# Revit family: 280 NonAutomatic Series
name_source: partatom
category: Mechanical Equipment
revit_build: Autodesk Revit 2013 (Build: 20120221_2030(x64)
units: mm (PartAtom-declared; Revit-internal decimal feet)

## types (13) — shared parameters
Assembly Code = D2010900
Cooling = Oil Filled
Cord Length = 180"
Cord Type = UL listed, 3-wire neoprene cord and plug (1 Ph) or 4-wire cord with no plug (3 Ph)
Default Elevation = 0"
Description = Single Seal Non-Automatic Submersible Sewage or Dewatering Pumps
Discharge Diameter = 2" or 3" NPT Female, Flanged Vertical
Discharge Height = 6 1/4"
Discharge Radius = 1"
Height = 19 9/16"
Hertz = 60
Impeller = Cast Iron
Impeller Type = Non-clogging vortex
Installation Type = Floor Mounted
Insulation = Class B
Lead Wires Insulation = Class B
Length = 13 9/16"
Manufacturer = Zoeller
Masterformat Number = 33 36 16
Masterformat Title = Utility Septic Tank Effluent Pumps
Material = Cast Iron-Zoeller-Powder Coated Epoxy
Max. Operating Temp. = 130.00 °F
Mechanical Seals = Carbon and Ceramic
Minimum Head = 60"
Motor Thermal Shutoff (Single Phase Only) = Thermal Overload Sensors With Automatic Reset.
Motor Type = Submersible
Omniclass Table 23 Code = 23.60.30.21
Omniclass Table 23 Title = Pumps
Operation = Non-Automatic
Price = Prices may vary. Please consult Manufacturer Representative for most up-to-date price list.
Product Page URL = http://www.zoellerpumps.com
RPM = 1725
Shipping Weight = 80 lbs
Solid Handling = 2" Spherical Solids
Square Ring & Gasket = Neoprene
Type Comments = Available in single or double seal designs.
URL = http://www.zoellerpumps.com
Warranty Information = 36 Months (Limited)
Waste Connection = Yes
Width = 10"

## per-type parameters (varying)
| type | Amps | Apparent Load | Flow @ 5' | Maximum Head | Model | Motor | Phase | Type | Voltage |
| 282-115V 1Ph | 10 A | 1185 VA | 127 GPM | 312" | 282 | 1/2 HP | 1 | Permanent Split Capacitor | 115 V |
| 282-230V 1Ph | 5 A | 1150 VA | 127 GPM | 312" | 282 | 1/2 HP | 1 | Permanent Split Capacitor | 230 V |
| 282-200V 1Ph | 6 A | 1220 VA | 127 GPM | 312" | 282 | 1/2 HP | 1 | Permanent Split Capacitor | 200 V |
| 282-200V 3Ph | 4 A | 720 VA | 127 GPM | 312" | 282 | 1/2 HP | 3 Ph | 3 Phase | 200 V |
| 282-230V 3Ph | 3 A | 690 VA | 127 GPM | 312" | 282 | 1/2 HP | 3 Ph | 3 Phase | 230 V |
| 282-460V 3Ph | 2 A | 782 VA | 127 GPM | 312" | 282 | 1/2 HP | 3 Ph | 3 Phase | 460 V |
| 282-575V 3Ph | 1 A | 805 VA | 127 GPM | 312" | 282 | 1/2 HP | 3 Ph | 3 Phase | 575 V |
| 284-230V 1Ph | 9 A | 2047 VA | 179 GPM | 420" | 284 | 1 HP | 1 | Permanent Split Capacitor | 230 V |
| 284-200V 1Ph | 9 A | 1860 VA | 179 GPM | 420" | 284 | 1 HP | 1 | Permanent Split Capacitor | 200 V |
| 284-200V 3Ph | 6 A | 1100 VA | 179 GPM | 420" | 284 | 1 HP | 3 Ph | 3 Phase | 200 V |
| 284-230V 3Ph | 5 A | 1150 VA | 179 GPM | 420" | 284 | 1 HP | 3 Ph | 3 Phase | 230 V |
| 284-460V 3Ph | 3 A | 1196 VA | 179 GPM | 420" | 284 | 1 HP | 3 Ph | 3 Phase | 460 V |
| 284-575V 3Ph | 2 A | 1265 VA | 179 GPM | 420" | 284 | 1 HP | 3 Ph | 3 Phase | 575 V |

## geometry (parser evidence)
native form markers: Blend x6, Sweep x3
no freeform markers — native parametric forms only
